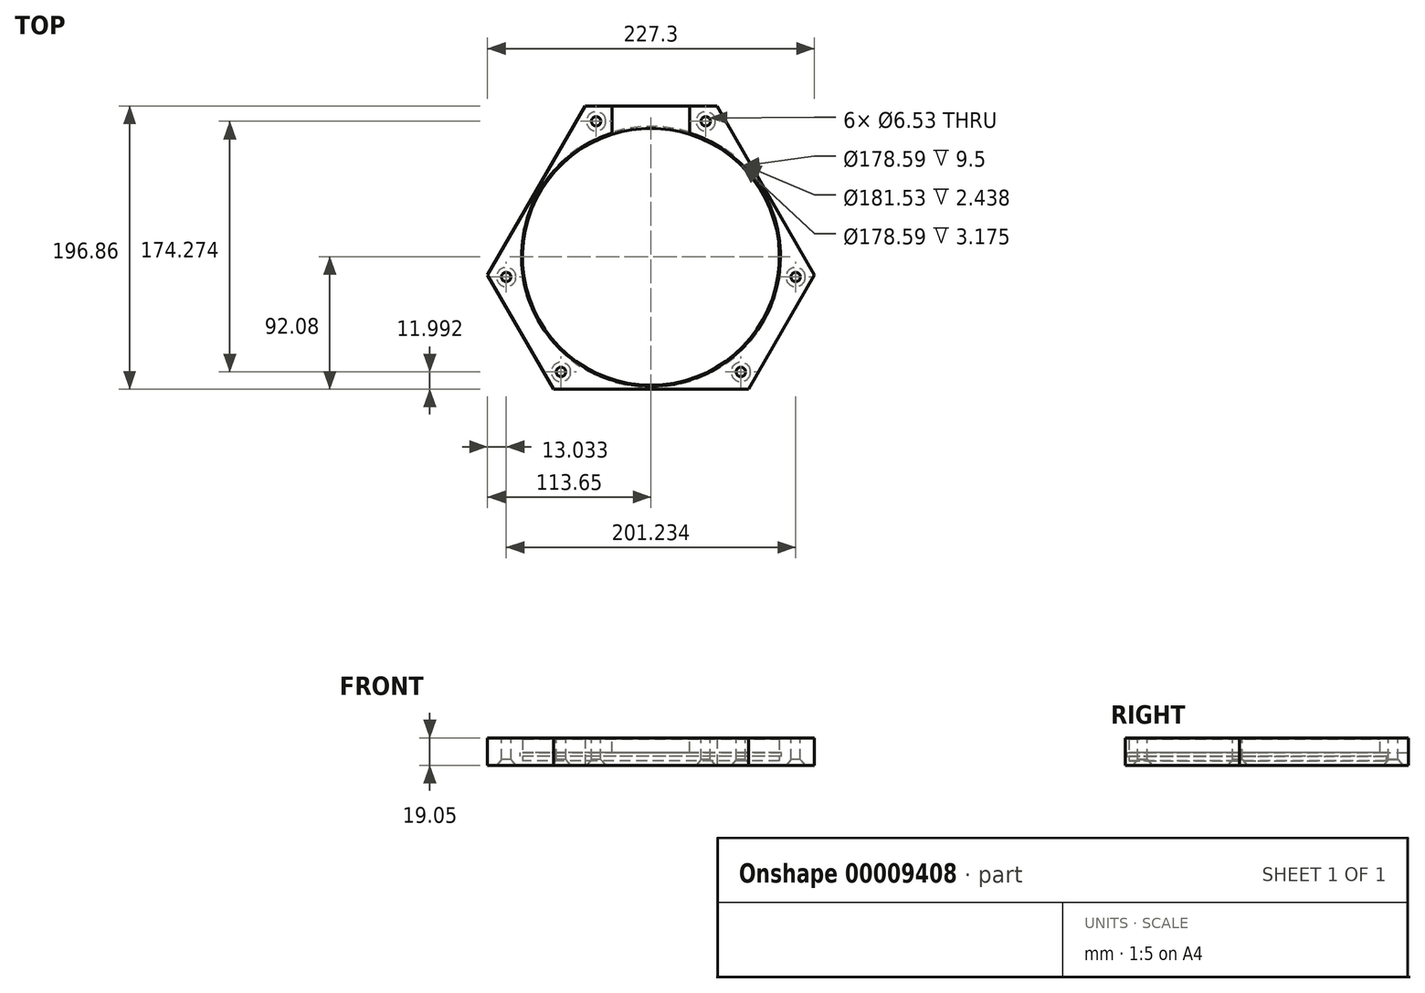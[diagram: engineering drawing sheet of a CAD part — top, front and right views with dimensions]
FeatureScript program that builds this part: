
annotation { "Feature Type Name" : "Feature", "Feature Type Description" : "" }
export const myFeature = defineFeature(function(context is Context, id is Id, definition is map)
    precondition{}
    {
        {
            var Q0;
            Q0=qCreatedBy(makeId("Top.planeOp"),FACE);
            var sketch = newSketch(context, id + "F0", { "sketchPlane" : qUnion([Q0])});
            skCircle(sketch, "E0", {"center": v(0, 0) * mm, "radius": 89.3 * mm});
            skCircle(sketch, "E1.cCircle", {"center": v(0, 0) * mm, "radius": 92.07 * mm, "construction": true});
            skLineSegment(sketch, "E1.0", {"start": v(19.02, 151.2) * mm, "end": v(140.46, -59.13) * mm});
            skLineSegment(sketch, "E1.1", {"start": v(121.44, -92.07) * mm, "end": v(-121.44, -92.08) * mm});
            skLineSegment(sketch, "E1.2", {"start": v(-140.46, -59.13) * mm, "end": v(-19.02, 151.2) * mm});
            skPoint(sketch, "E1.0.midPoint", {"position": v(79.74, 46.04) * mm});
            skArc(sketch, "E2", {"start": v(-140.46, -59.13) * mm, "mid": v(-131.98, -76.2) * mm, "end": v(-121.44, -92.07) * mm});
            skPoint(sketch, "E3.orphan", {"position": v(0, 184.15) * mm});
            skArc(sketch, "E4.trimOffspring", {"start": v(19.02, 151.2) * mm, "mid": v(0, 152.4) * mm, "end": v(-19.02, 151.2) * mm});
            skArc(sketch, "E5.trimOffspring", {"start": v(121.44, -92.08) * mm, "mid": v(131.98, -76.2) * mm, "end": v(140.46, -59.13) * mm});
            skPoint(sketch, "E6.orphan", {"position": v(159.48, -92.08) * mm});
            skPoint(sketch, "E7.orphan", {"position": v(-159.48, -92.07) * mm});
            skSolve(sketch);
        }
        {
            var Q0;
            Q0=makeQuery(id+"F0.imprint","IMPRINT",FACE,{"disambiguationData":[TD([[makeQuery(id+"F0.imprint","IMPRINT",EDGE,{"derivedFrom":sQuery(id+"F0.wireOp",EDGE,"E0")}),1.0]])]});
            extrude(context, id + "F1", {"entities" : qUnion([Q0]), "depth" : 3.17 * mm, "offsetDistance" : 25.4 * mm});
        }
        {
            var Q0;
            Q0=makeQuery(id+"F0.imprint","IMPRINT",FACE,{"disambiguationData":[TD([[makeQuery(id+"F0.imprint","IMPRINT",EDGE,{"derivedFrom":sQuery(id+"F0.wireOp",EDGE,"E0")}),-1.0]])]});
            extrude(context, id + "F2", {"entities" : qUnion([Q0]), "operationType" : NewBodyOperationType.ADD, "depth" : 19.05 * mm, "offsetDistance" : 25.4 * mm});
        }
        {
            var Q0;
            Q0=qCreatedBy(makeId("Top.planeOp"),FACE);
            var sketch = newSketch(context, id + "F3", { "sketchPlane" : qUnion([Q0])});
            skPoint(sketch, "E8.0", {"position": v(0, 0) * mm});
            skCircle(sketch, "E9.cCircle", {"center": v(0, 0) * mm, "radius": 127 * mm, "construction": true});
            skLineSegment(sketch, "E9.0", {"start": v(0, 127) * mm, "end": v(109.99, -63.5) * mm});
            skLineSegment(sketch, "E9.1", {"start": v(109.99, -63.5) * mm, "end": v(-109.99, -63.5) * mm});
            skLineSegment(sketch, "E9.2", {"start": v(-109.99, -63.5) * mm, "end": v(0, 127) * mm});
            skSolve(sketch);
        }
        {
            var Q0;
            Q0=sQuery(id+"F3.wireOp",VERTEX,"E9.0.end");
            var Q1;
            Q1=sQuery(id+"F3.wireOp",VERTEX,"E9.0.start");
            var Q2;
            Q2=sQuery(id+"F3.wireOp",VERTEX,"E9.1.end");
            var Q3;
            Q3=makeQuery(id+"F1.opExtrude","SWEPT_BODY",BODY,{"disambiguationData":[OSD([sQuery(id+"F0.wireOp",EDGE,"E0")])]});
            hole(context, id + "F4", {"style" : HoleStyle.SIMPLE, "endStyle" : HoleEndStyle.THROUGH, "oppositeDirection" : true, "holeDiameter" : 12.95 * mm, "majorDiameter" : 3.5 * mm, "isTappedThrough" : true, "tappedDepth" : 12.7 * mm, "tapClearance" : 3, "locations" : qUnion([Q0, Q1, Q2]), "scope" : qUnion([Q3])});
        }
        {
            var Q0;
            Q0=qCreatedBy(makeId("Top.planeOp"),FACE);
            var sketch = newSketch(context, id + "F5", { "sketchPlane" : qUnion([Q0])});
            skPoint(sketch, "E10.0", {"position": v(0, 0) * mm});
            skCircle(sketch, "E11.cCircle", {"center": v(0, 0) * mm, "radius": 101.6 * mm, "construction": true});
            skLineSegment(sketch, "E11.0", {"start": v(-38.1, 94.19) * mm, "end": v(100.62, -14.1) * mm});
            skLineSegment(sketch, "E11.1", {"start": v(100.62, -14.1) * mm, "end": v(-62.52, -80.09) * mm});
            skLineSegment(sketch, "E11.2", {"start": v(-62.52, -80.09) * mm, "end": v(-38.1, 94.19) * mm});
            skLineSegment(sketch, "E12.0", {"start": v(38.1, 94.19) * mm, "end": v(62.52, -80.09) * mm});
            skLineSegment(sketch, "E12.1", {"start": v(62.52, -80.09) * mm, "end": v(-100.62, -14.1) * mm});
            skLineSegment(sketch, "E12.2", {"start": v(-100.62, -14.1) * mm, "end": v(38.1, 94.19) * mm});
            skCircle(sketch, "E13.0", {"center": v(0, 127) * mm, "radius": 6.48 * mm});
            skLineSegment(sketch, "E14", {"start": v(0, 0) * mm, "end": v(0, 127) * mm, "construction": true});
            skSolve(sketch);
        }
        {
            var Q0;
            Q0=sQuery(id+"F5.wireOp",VERTEX,"E11.0.end");
            var Q1;
            Q1=sQuery(id+"F5.wireOp",VERTEX,"E12.0.end");
            var Q2;
            Q2=sQuery(id+"F5.wireOp",VERTEX,"E11.1.end");
            var Q3;
            Q3=sQuery(id+"F5.wireOp",VERTEX,"E12.1.end");
            var Q4;
            Q4=sQuery(id+"F5.wireOp",VERTEX,"E11.0.start");
            var Q5;
            Q5=sQuery(id+"F5.wireOp",VERTEX,"E12.0.start");
            var Q6;
            Q6=makeQuery(id+"F1.opExtrude","SWEPT_BODY",BODY,{"disambiguationData":[OSD([sQuery(id+"F0.wireOp",EDGE,"E0")])]});
            hole(context, id + "F6", {"style" : HoleStyle.C_SINK, "endStyle" : HoleEndStyle.THROUGH, "oppositeDirection" : true, "holeDiameter" : 6.53 * mm, "cSinkDiameter" : 13.5 * mm, "cSinkAngle" : 82 * degree, "majorDiameter" : 6.35 * mm, "isTappedThrough" : true, "tappedDepth" : 12.7 * mm, "tapClearance" : 3, "locations" : qUnion([Q0, Q1, Q2, Q3, Q4, Q5]), "scope" : qUnion([Q6])});
        }
        {
            var Q0;
            Q0=qCreatedBy(makeId("Front.planeOp"),FACE);
            cPlane(context, id + "F7", {"entities" : qUnion([Q0]), "cplaneType" : CPlaneType.OFFSET, "offset" : 104.77 * mm, "oppositeDirection" : true, "width" : 152.4 * mm, "height" : 152.4 * mm});
        }
        {
            var Q0;
            Q0=qCreatedBy(makeId("Top.planeOp"),FACE);
            var sketch = newSketch(context, id + "F8", { "sketchPlane" : qUnion([Q0])});
            skLineSegment(sketch, "E15", {"start": v(45.83, 104.78) * mm, "end": v(-45.83, 104.78) * mm});
            skLineSegment(sketch, "E16.1.0", {"start": v(-113.65, -12.7) * mm, "end": v(-67.82, -92.08) * mm});
            skLineSegment(sketch, "E16.2.0", {"start": v(67.82, -92.08) * mm, "end": v(113.65, -12.7) * mm});
            skPoint(sketch, "E16.center", {"position": v(0, 0) * mm});
            skArc(sketch, "E17.0.3", {"start": v(140.46, -59.13) * mm, "mid": v(131.98, -76.2) * mm, "end": v(121.44, -92.08) * mm});
            skLineSegment(sketch, "E17.0.4", {"start": v(121.44, -92.07) * mm, "end": v(-121.44, -92.08) * mm});
            skArc(sketch, "E17.0.5", {"start": v(-121.44, -92.08) * mm, "mid": v(-131.98, -76.2) * mm, "end": v(-140.46, -59.13) * mm});
            skLineSegment(sketch, "E18.0", {"start": v(19.02, 151.2) * mm, "end": v(140.46, -59.13) * mm});
            skLineSegment(sketch, "E19.0", {"start": v(-140.46, -59.13) * mm, "end": v(-19.02, 151.2) * mm});
            skArc(sketch, "E20.0", {"start": v(19.02, 151.2) * mm, "mid": v(0, 152.4) * mm, "end": v(-19.02, 151.2) * mm});
            skSolve(sketch);
        }
        {
            var Q0;
            {var subQ0=sQuery(id+"F8.wireOp",EDGE,"E16.1.0");Q0=makeQuery(id+"F8.imprint","IMPRINT",FACE,{"disambiguationData":[TD([[makeQuery(id+"F8.imprint","IMPRINT",EDGE,{"derivedFrom":subQ0}),-1.0]])]});}
            var Q1;
            {var subQ0=sQuery(id+"F8.wireOp",EDGE,"E16.2.0");Q1=makeQuery(id+"F8.imprint","IMPRINT",FACE,{"disambiguationData":[TD([[makeQuery(id+"F8.imprint","IMPRINT",EDGE,{"derivedFrom":subQ0}),-1.0]])]});}
            var Q2;
            {var subQ0=sQuery(id+"F8.wireOp",EDGE,"E15");Q2=makeQuery(id+"F8.imprint","IMPRINT",FACE,{"disambiguationData":[TD([[makeQuery(id+"F8.imprint","IMPRINT",EDGE,{"derivedFrom":subQ0}),-1.0]])]});}
            extrude(context, id + "F9", {"entities" : qUnion([Q0, Q1, Q2]), "operationType" : NewBodyOperationType.REMOVE, "depth" : 25.4 * mm, "offsetDistance" : 25.4 * mm});
        }
        {
            var Q0;
            Q0=makeQuery(id+"F2.opExtrude","CAP_FACE",FACE,{"disambiguationData":[OSD([sQuery(id+"F0.wireOp",EDGE,"E0"),sQuery(id+"F0.wireOp",EDGE,"E1.0"),sQuery(id+"F0.wireOp",EDGE,"E1.1"),sQuery(id+"F0.wireOp",EDGE,"E1.2"),sQuery(id+"F0.wireOp",EDGE,"E2"),sQuery(id+"F0.wireOp",EDGE,"E4.trimOffspring"),sQuery(id+"F0.wireOp",EDGE,"E5.trimOffspring")])],"isStart":false});
            var sketch = newSketch(context, id + "F10", { "sketchPlane" : qUnion([Q0])});
            skCircle(sketch, "E21.0", {"center": v(0, 0) * mm, "radius": 89.3 * mm});
            skLineSegment(sketch, "E22.0", {"start": v(-45.83, 104.78) * mm, "end": v(45.83, 104.78) * mm});
            skLineSegment(sketch, "E23", {"start": v(-26.99, 85.12) * mm, "end": v(-26.99, 104.78) * mm});
            skLineSegment(sketch, "E24", {"start": v(26.99, 104.78) * mm, "end": v(26.99, 85.12) * mm});
            skSolve(sketch);
        }
        {
            var Q0;
            {var subQ0=sQuery(id+"F10.wireOp",EDGE,"E23");Q0=makeQuery(id+"F10.imprint","IMPRINT",FACE,{"disambiguationData":[TD([[makeQuery(id+"F10.imprint","IMPRINT",EDGE,{"derivedFrom":subQ0}),-1.0]])]});}
            extrude(context, id + "F11", {"entities" : qUnion([Q0]), "operationType" : NewBodyOperationType.REMOVE, "oppositeDirection" : true, "depth" : 10.16 * mm, "offsetDistance" : 25.4 * mm});
        }
        {
            var Q0;
            Q0=qCreatedBy(makeId("Front.planeOp"),FACE);
            var sketch = newSketch(context, id + "F12", { "sketchPlane" : qUnion([Q0])});
            skLineSegment(sketch, "E25", {"start": v(-89.3, 19.05) * mm, "end": v(-106.32, 19.05) * mm, "construction": true});
            skLineSegment(sketch, "E26", {"start": v(106.32, 19.05) * mm, "end": v(89.3, 19.05) * mm, "construction": true});
            skLineSegment(sketch, "E27", {"start": v(89.3, 19.05) * mm, "end": v(89.3, 3.18) * mm, "construction": true});
            skLineSegment(sketch, "E28", {"start": v(-89.3, 3.18) * mm, "end": v(-89.3, 19.05) * mm, "construction": true});
            skLineSegment(sketch, "E29.bottom", {"start": v(-89.3, 6.35) * mm, "end": v(-90.77, 6.35) * mm});
            skLineSegment(sketch, "E29.top", {"start": v(-89.3, 8.79) * mm, "end": v(-90.77, 8.79) * mm});
            skLineSegment(sketch, "E29.left", {"start": v(-89.3, 6.35) * mm, "end": v(-89.3, 8.79) * mm});
            skLineSegment(sketch, "E29.right", {"start": v(-90.77, 6.35) * mm, "end": v(-90.77, 8.79) * mm});
            skLineSegment(sketch, "E30", {"start": v(0, 0) * mm, "end": v(0, 43.82) * mm, "construction": true});
            skSolve(sketch);
        }
        {
            var Q0;
            Q0=makeQuery(id+"F12.imprint","IMPRINT",FACE,{"disambiguationData":[TD([[makeQuery(id+"F12.imprint","IMPRINT",EDGE,{"derivedFrom":sQuery(id+"F12.wireOp",EDGE,"E29.bottom")}),-1.0]])]});
            var Q1;
            Q1=sQuery(id+"F12.wireOp",EDGE,"E30");
            revolve(context, id + "F13", {"operationType" : NewBodyOperationType.REMOVE, "surfaceOperationType" : NewSurfaceOperationType.NEW, "entities" : qUnion([Q0]), "axis" : qUnion([Q1]), "revolveType" : RevolveType.FULL, "oppositeDirection" : true});
        }
        {
            var Q0;
            Q0=makeQuery(id+"F2.opExtrude","CAP_EDGE",EDGE,{"disambiguationData":[OSD([sQuery(id+"F0.wireOp",EDGE,"E0")])],"isStart":false});
            chamfer(context, id + "F14", {"entities" : qUnion([Q0]), "width" : 0.76 * mm, "tangentPropagation" : true});
        }
    });
